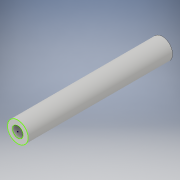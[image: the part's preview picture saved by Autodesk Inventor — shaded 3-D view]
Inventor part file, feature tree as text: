
AUTODESK INVENTOR PART (.ipt)
format: ipt  version: 2017 (Build 210142000, 142)  size: 95,232 bytes
history: native  units: in
note: dims shown in document units (in); Inventor stores cm internally (conversion verified against a paired STEP export)
features: sketch x2, extrude x1
ambient origin geometry x8: Origin, YZ Plane, XZ Plane, XY Plane, X Axis, Y Axis, Z Axis, Center Point
bodies: Solid1 (feature_tree)
feature tree (3):
  extrude  "Extrusion1"  [1 undecoded]
  sketch  "Sketch3"
  sketch  "Sketch1"  dims[d0=3.5in d1=0.0in]
note: 1 required parameter value undecoded (feature->parameter linkage not recoverable at this tier; creation-order binding heuristic only, values carry confidence <= 0.55)
